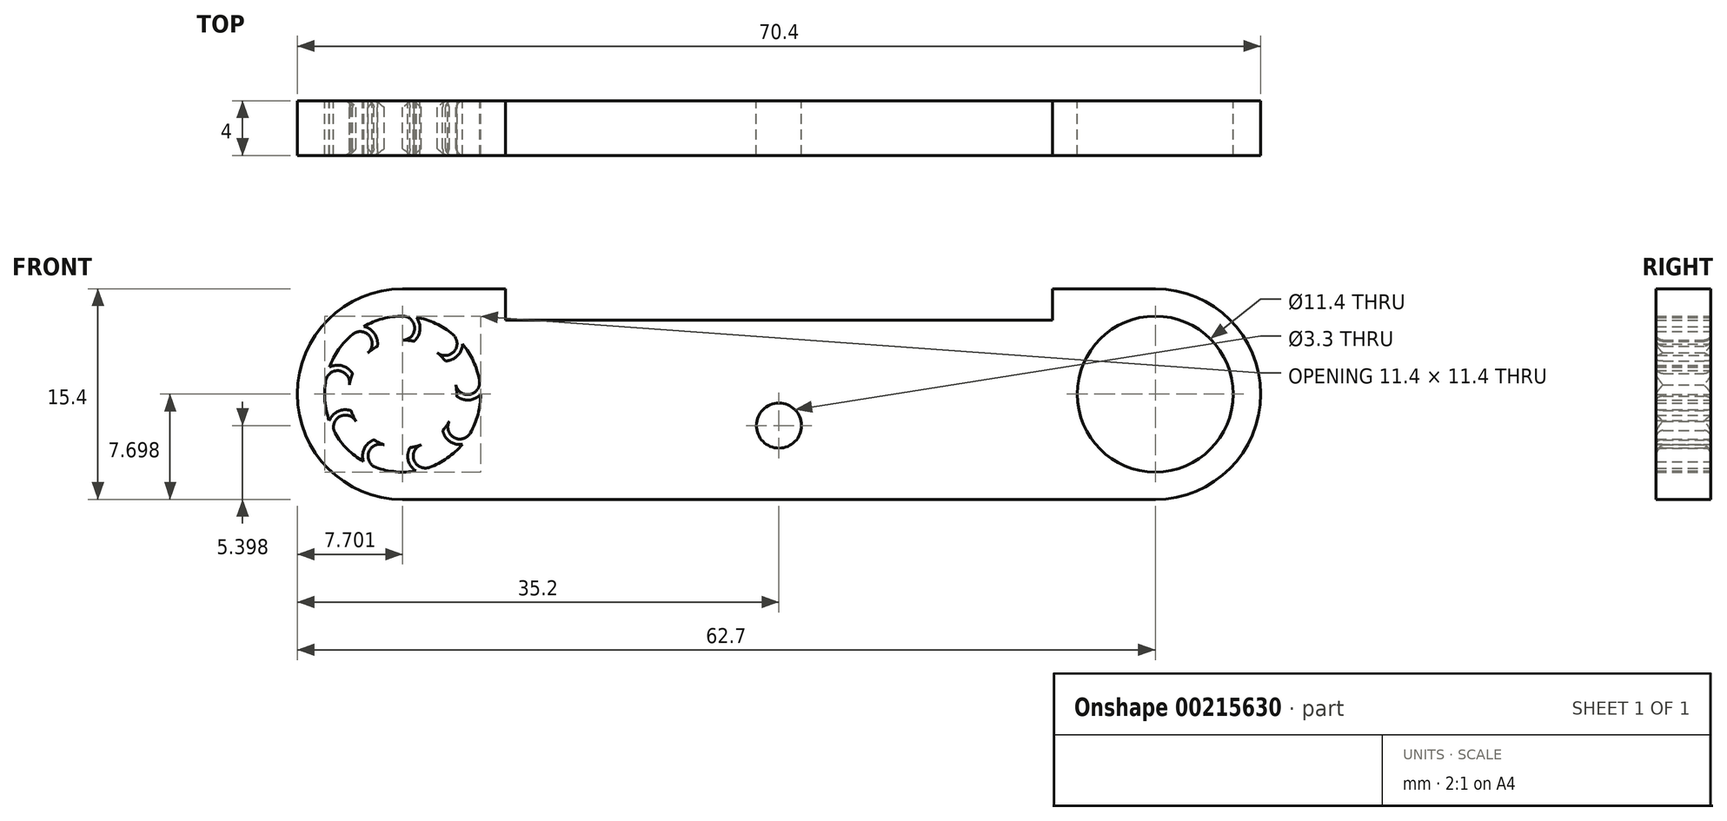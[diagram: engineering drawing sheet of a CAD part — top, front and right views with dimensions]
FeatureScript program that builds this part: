
annotation { "Feature Type Name" : "Feature", "Feature Type Description" : "" }
export const myFeature = defineFeature(function(context is Context, id is Id, definition is map)
    precondition{}
    {
        {
            var Q0;
            Q0=qCreatedBy(makeId("Front.planeOp"),FACE);
            var sketch = newSketch(context, id + "F0", { "sketchPlane" : qUnion([Q0])});
            skLineSegment(sketch, "E0", {"start": v(-27.5, -12.7) * mm, "end": v(0, -12.7) * mm});
            skLineSegment(sketch, "E1", {"start": v(0, -12.7) * mm, "end": v(27.5, -12.7) * mm});
            skCircle(sketch, "E2", {"center": v(-27.5, -12.7) * mm, "radius": 3.8 * mm});
            skCircle(sketch, "E3", {"center": v(27.5, -12.7) * mm, "radius": 3.8 * mm, "construction": true});
            skCircle(sketch, "E4", {"center": v(-27.5, -12.7) * mm, "radius": 5.7 * mm});
            skCircle(sketch, "E5", {"center": v(27.5, -12.7) * mm, "radius": 5.7 * mm});
            skCircle(sketch, "E6", {"center": v(-27.5, -12.7) * mm, "radius": 7.7 * mm});
            skCircle(sketch, "E7", {"center": v(27.5, -12.7) * mm, "radius": 7.7 * mm});
            skLineSegment(sketch, "E8", {"start": v(-27.5, -8.9) * mm, "end": v(-27.5, -7) * mm, "construction": true});
            skLineSegment(sketch, "E9.bottom", {"start": v(-27.5, -5) * mm, "end": v(27.5, -5) * mm});
            skPoint(sketch, "E10", {"position": v(0, -5) * mm});
            skLineSegment(sketch, "E11", {"start": v(27.5, -20.4) * mm, "end": v(-27.5, -20.4) * mm});
            skSolve(sketch);
        }
        {
            var Q0;
            Q0=qSketchRegion(id+"F0",true);
            extrude(context, id + "F1", {"entities" : qUnion([Q0]), "depth" : (4) * mm});
        }
        {
            var Q0;
            Q0=makeQuery(id+"F1.opExtrude","CAP_FACE",FACE,{"disambiguationData":[OSD([sQuery(id+"F0.wireOp",EDGE,"E4"),sQuery(id+"F0.wireOp",EDGE,"E5"),sQuery(id+"F0.wireOp",EDGE,"E6"),sQuery(id+"F0.wireOp",EDGE,"E7"),sQuery(id+"F0.wireOp",EDGE,"E9.bottom"),sQuery(id+"F0.wireOp",EDGE,"E9.top"),sQuery(id+"F0.wireOp",EDGE,"E9.left"),sQuery(id+"F0.wireOp",EDGE,"E9.right")])],"isStart":true});
            var sketch = newSketch(context, id + "F2", { "sketchPlane" : qUnion([Q0])});
            skCircle(sketch, "E12.0", {"center": v(27.5, -12.7) * mm, "radius": 5.7 * mm});
            skCircle(sketch, "E13", {"center": v(27.5, -12.7) * mm, "radius": 3.95 * mm});
            skLineSegment(sketch, "E14", {"start": v(27.5, -12.7) * mm, "end": v(27.5, -7) * mm, "construction": true});
            skArc(sketch, "E15", {"start": v(27.5, -7) * mm, "mid": v(26.62, -7.87) * mm, "end": v(27.5, -8.74) * mm});
            skArc(sketch, "E16", {"start": v(27.5, -6.6) * mm, "mid": v(26.3, -7.42) * mm, "end": v(26.67, -8.83) * mm});
            skArc(sketch, "E17.1.0", {"start": v(23.58, -8.02) * mm, "mid": v(23.2, -9.42) * mm, "end": v(24.38, -10.27) * mm});
            skArc(sketch, "E17.1.1", {"start": v(23.84, -8.33) * mm, "mid": v(23.73, -9.56) * mm, "end": v(24.96, -9.67) * mm});
            skArc(sketch, "E17.2.0", {"start": v(21.5, -11.63) * mm, "mid": v(22.1, -12.95) * mm, "end": v(23.55, -12.84) * mm});
            skArc(sketch, "E17.2.1", {"start": v(21.89, -11.7) * mm, "mid": v(22.6, -12.72) * mm, "end": v(23.61, -12) * mm});
            skArc(sketch, "E17.3.0", {"start": v(22.22, -15.74) * mm, "mid": v(23.53, -16.36) * mm, "end": v(24.57, -15.35) * mm});
            skArc(sketch, "E17.3.1", {"start": v(22.56, -15.54) * mm, "mid": v(23.76, -15.86) * mm, "end": v(24.08, -14.67) * mm});
            skArc(sketch, "E17.4.0", {"start": v(25.41, -18.42) * mm, "mid": v(26.82, -18.05) * mm, "end": v(26.96, -16.6) * mm});
            skArc(sketch, "E17.4.1", {"start": v(25.55, -18.05) * mm, "mid": v(26.67, -17.53) * mm, "end": v(26.15, -16.4) * mm});
            skArc(sketch, "E17.5.0", {"start": v(29.59, -18.42) * mm, "mid": v(30.43, -17.24) * mm, "end": v(29.6, -16.04) * mm});
            skArc(sketch, "E17.5.1", {"start": v(29.45, -18.05) * mm, "mid": v(29.97, -16.93) * mm, "end": v(28.85, -16.4) * mm});
            skArc(sketch, "E17.6.0", {"start": v(32.78, -15.74) * mm, "mid": v(32.66, -14.3) * mm, "end": v(31.26, -13.9) * mm});
            skArc(sketch, "E17.6.1", {"start": v(32.44, -15.54) * mm, "mid": v(32.12, -14.35) * mm, "end": v(30.92, -14.67) * mm});
            skArc(sketch, "E17.7.0", {"start": v(33.5, -11.63) * mm, "mid": v(32.48, -10.6) * mm, "end": v(31.16, -11.2) * mm});
            skArc(sketch, "E17.7.1", {"start": v(33.11, -11.7) * mm, "mid": v(32.1, -11) * mm, "end": v(31.39, -12) * mm});
            skArc(sketch, "E17.8.0", {"start": v(31.42, -8.02) * mm, "mid": v(29.97, -7.89) * mm, "end": v(29.34, -9.2) * mm});
            skArc(sketch, "E17.8.1", {"start": v(31.16, -8.33) * mm, "mid": v(29.93, -8.43) * mm, "end": v(30.04, -9.67) * mm});
            skSolve(sketch);
        }
        {
            var Q0;
            {var subQ0=sQuery(id+"F2.wireOp",EDGE,"E15");Q0=makeQuery(id+"F2.imprint","IMPRINT",FACE,{"disambiguationData":[TD([[makeQuery(id+"F2.imprint","IMPRINT",EDGE,{"derivedFrom":subQ0}),-1.0]])]});}
            var Q1;
            {var subQ0=sQuery(id+"F2.wireOp",EDGE,"E17.1.1");Q1=makeQuery(id+"F2.imprint","IMPRINT",FACE,{"disambiguationData":[TD([[makeQuery(id+"F2.imprint","IMPRINT",EDGE,{"derivedFrom":subQ0}),-1.0]])]});}
            var Q2;
            {var subQ0=sQuery(id+"F2.wireOp",EDGE,"E17.2.1");Q2=makeQuery(id+"F2.imprint","IMPRINT",FACE,{"disambiguationData":[TD([[makeQuery(id+"F2.imprint","IMPRINT",EDGE,{"derivedFrom":subQ0}),-1.0]])]});}
            var Q3;
            {var subQ0=sQuery(id+"F2.wireOp",EDGE,"E17.3.1");Q3=makeQuery(id+"F2.imprint","IMPRINT",FACE,{"disambiguationData":[TD([[makeQuery(id+"F2.imprint","IMPRINT",EDGE,{"derivedFrom":subQ0}),-1.0]])]});}
            var Q4;
            {var subQ0=sQuery(id+"F2.wireOp",EDGE,"E17.4.1");Q4=makeQuery(id+"F2.imprint","IMPRINT",FACE,{"disambiguationData":[TD([[makeQuery(id+"F2.imprint","IMPRINT",EDGE,{"derivedFrom":subQ0}),-1.0]])]});}
            var Q5;
            {var subQ0=sQuery(id+"F2.wireOp",EDGE,"E17.5.1");Q5=makeQuery(id+"F2.imprint","IMPRINT",FACE,{"disambiguationData":[TD([[makeQuery(id+"F2.imprint","IMPRINT",EDGE,{"derivedFrom":subQ0}),-1.0]])]});}
            var Q6;
            {var subQ0=sQuery(id+"F2.wireOp",EDGE,"E17.6.1");Q6=makeQuery(id+"F2.imprint","IMPRINT",FACE,{"disambiguationData":[TD([[makeQuery(id+"F2.imprint","IMPRINT",EDGE,{"derivedFrom":subQ0}),-1.0]])]});}
            var Q7;
            {var subQ0=sQuery(id+"F2.wireOp",EDGE,"E17.7.1");Q7=makeQuery(id+"F2.imprint","IMPRINT",FACE,{"disambiguationData":[TD([[makeQuery(id+"F2.imprint","IMPRINT",EDGE,{"derivedFrom":subQ0}),-1.0]])]});}
            var Q8;
            {var subQ0=sQuery(id+"F2.wireOp",EDGE,"E17.8.1");Q8=makeQuery(id+"F2.imprint","IMPRINT",FACE,{"disambiguationData":[TD([[makeQuery(id+"F2.imprint","IMPRINT",EDGE,{"derivedFrom":subQ0}),-1.0]])]});}
            var Q9;
            Q9=makeQuery(id+"F1.opExtrude","CAP_FACE",FACE,{"disambiguationData":[OSD([sQuery(id+"F0.wireOp",EDGE,"E4"),sQuery(id+"F0.wireOp",EDGE,"E5"),sQuery(id+"F0.wireOp",EDGE,"E6"),sQuery(id+"F0.wireOp",EDGE,"E7"),sQuery(id+"F0.wireOp",EDGE,"E9.bottom"),sQuery(id+"F0.wireOp",EDGE,"E9.top"),sQuery(id+"F0.wireOp",EDGE,"E9.left"),sQuery(id+"F0.wireOp",EDGE,"E9.right")])],"isStart":false});
            extrude(context, id + "F3", {"entities" : qUnion([Q0, Q1, Q2, Q3, Q4, Q5, Q6, Q7, Q8]), "operationType" : NewBodyOperationType.ADD, "endBound" : BoundingType.UP_TO_SURFACE, "oppositeDirection" : true, "endBoundEntityFace" : qUnion([Q9]), "depth" : 25 * mm});
        }
        {
            var Q0;
            {var subQ0=sQuery(id+"F2.wireOp",EDGE,"E17.2.1");var subQ1=sQuery(id+"F2.wireOp",EDGE,"E17.2.0");var subQ2=sQuery(id+"F2.wireOp",EDGE,"E13");var subQ3=sQuery(id+"F2.wireOp",EDGE,"E12.0");var subQ4=sQuery(id+"F2.wireOp",EDGE,"E17.3.1");var subQ5=sQuery(id+"F2.wireOp",EDGE,"E17.3.0");var subQ6=sQuery(id+"F2.wireOp",EDGE,"E17.4.1");var subQ7=sQuery(id+"F2.wireOp",EDGE,"E17.4.0");var subQ8=sQuery(id+"F2.wireOp",EDGE,"E17.5.1");var subQ9=sQuery(id+"F2.wireOp",EDGE,"E17.5.0");var subQ10=sQuery(id+"F2.wireOp",EDGE,"E17.6.1");var subQ11=sQuery(id+"F2.wireOp",EDGE,"E17.6.0");var subQ12=sQuery(id+"F2.wireOp",EDGE,"E17.7.1");var subQ13=sQuery(id+"F2.wireOp",EDGE,"E17.7.0");var subQ14=sQuery(id+"F2.wireOp",EDGE,"E17.8.1");var subQ15=sQuery(id+"F2.wireOp",EDGE,"E17.8.0");var subQ16=sQuery(id+"F2.wireOp",EDGE,"E16");var subQ17=sQuery(id+"F2.wireOp",EDGE,"E15");var subQ18=sQuery(id+"F2.wireOp",EDGE,"E17.1.1");var subQ19=sQuery(id+"F2.wireOp",EDGE,"E17.1.0");Q0=makeQuery(id+"FG6rSbF2kgmWDMH_1.1.F3.boolean.opBoolean","MERGE",FACE,{"derivedFrom":[makeQuery(id+"F3.boolean.opBoolean","MERGE",FACE,{"derivedFrom":[makeQuery(id+"F1.opExtrude","CAP_FACE",FACE,{"disambiguationData":[OSD([sQuery(id+"F0.wireOp",EDGE,"E0"),sQuery(id+"F0.wireOp",EDGE,"E1"),sQuery(id+"F0.wireOp",EDGE,"E4"),sQuery(id+"F0.wireOp",EDGE,"E5"),sQuery(id+"F0.wireOp",EDGE,"E6"),sQuery(id+"F0.wireOp",EDGE,"E7"),sQuery(id+"F0.wireOp",EDGE,"E9.bottom")])],"isStart":true}),makeQuery(id+"F3.opExtrude","CAP_FACE",FACE,{"disambiguationData":[OSD([subQ3,subQ2,subQ19,subQ18])],"isStart":true}),makeQuery(id+"F3.opExtrude","CAP_FACE",FACE,{"disambiguationData":[OSD([subQ3,subQ2,subQ17,subQ16])],"isStart":true}),makeQuery(id+"F3.opExtrude","CAP_FACE",FACE,{"disambiguationData":[OSD([subQ3,subQ2,subQ15,subQ14])],"isStart":true}),makeQuery(id+"F3.opExtrude","CAP_FACE",FACE,{"disambiguationData":[OSD([subQ3,subQ2,subQ13,subQ12])],"isStart":true}),makeQuery(id+"F3.opExtrude","CAP_FACE",FACE,{"disambiguationData":[OSD([subQ3,subQ2,subQ11,subQ10])],"isStart":true}),makeQuery(id+"F3.opExtrude","CAP_FACE",FACE,{"disambiguationData":[OSD([subQ3,subQ2,subQ9,subQ8])],"isStart":true}),makeQuery(id+"F3.opExtrude","CAP_FACE",FACE,{"disambiguationData":[OSD([subQ3,subQ2,subQ7,subQ6])],"isStart":true}),makeQuery(id+"F3.opExtrude","CAP_FACE",FACE,{"disambiguationData":[OSD([subQ3,subQ2,subQ5,subQ4])],"isStart":true}),makeQuery(id+"F3.opExtrude","CAP_FACE",FACE,{"disambiguationData":[OSD([subQ3,subQ2,subQ1,subQ0])],"isStart":true})]}),makeQuery(id+"FG6rSbF2kgmWDMH_1.1.F3.opExtrude","CAP_FACE",FACE,{"disambiguationData":[OSD([subQ3,subQ2,subQ19,subQ18])],"isStart":true}),makeQuery(id+"FG6rSbF2kgmWDMH_1.1.F3.opExtrude","CAP_FACE",FACE,{"disambiguationData":[OSD([subQ3,subQ2,subQ17,subQ16])],"isStart":true}),makeQuery(id+"FG6rSbF2kgmWDMH_1.1.F3.opExtrude","CAP_FACE",FACE,{"disambiguationData":[OSD([subQ3,subQ2,subQ15,subQ14])],"isStart":true}),makeQuery(id+"FG6rSbF2kgmWDMH_1.1.F3.opExtrude","CAP_FACE",FACE,{"disambiguationData":[OSD([subQ3,subQ2,subQ13,subQ12])],"isStart":true}),makeQuery(id+"FG6rSbF2kgmWDMH_1.1.F3.opExtrude","CAP_FACE",FACE,{"disambiguationData":[OSD([subQ3,subQ2,subQ11,subQ10])],"isStart":true}),makeQuery(id+"FG6rSbF2kgmWDMH_1.1.F3.opExtrude","CAP_FACE",FACE,{"disambiguationData":[OSD([subQ3,subQ2,subQ9,subQ8])],"isStart":true}),makeQuery(id+"FG6rSbF2kgmWDMH_1.1.F3.opExtrude","CAP_FACE",FACE,{"disambiguationData":[OSD([subQ3,subQ2,subQ7,subQ6])],"isStart":true}),makeQuery(id+"FG6rSbF2kgmWDMH_1.1.F3.opExtrude","CAP_FACE",FACE,{"disambiguationData":[OSD([subQ3,subQ2,subQ5,subQ4])],"isStart":true}),makeQuery(id+"FG6rSbF2kgmWDMH_1.1.F3.opExtrude","CAP_FACE",FACE,{"disambiguationData":[OSD([subQ3,subQ2,subQ1,subQ0])],"isStart":true})]});}
            var sketch = newSketch(context, id + "F4", { "sketchPlane" : qUnion([Q0])});
            skLineSegment(sketch, "E18.bottom", {"start": v(-20, -5) * mm, "end": v(20, -5) * mm});
            skLineSegment(sketch, "E18.top", {"start": v(-20, -7.3) * mm, "end": v(20, -7.3) * mm});
            skLineSegment(sketch, "E18.left", {"start": v(-20, -5) * mm, "end": v(-20, -7.3) * mm});
            skLineSegment(sketch, "E18.right", {"start": v(20, -5) * mm, "end": v(20, -7.3) * mm});
            skSolve(sketch);
        }
        {
            var Q0;
            Q0 = qSketchRegion(id + "F4", true);
            extrude(context, id + "F5", {"entities" : qUnion([Q0]), "operationType" : NewBodyOperationType.REMOVE, "endBound" : BoundingType.THROUGH_ALL, "oppositeDirection" : true, "depth" : 25 * mm});
        }
        {
            var Q0;
            {var subQ0=sQuery(id+"F2.wireOp",EDGE,"E17.2.1");var subQ1=sQuery(id+"F2.wireOp",EDGE,"E17.2.0");var subQ2=sQuery(id+"F2.wireOp",EDGE,"E13");var subQ3=sQuery(id+"F2.wireOp",EDGE,"E12.0");var subQ4=sQuery(id+"F2.wireOp",EDGE,"E17.3.1");var subQ5=sQuery(id+"F2.wireOp",EDGE,"E17.3.0");var subQ6=sQuery(id+"F2.wireOp",EDGE,"E17.4.1");var subQ7=sQuery(id+"F2.wireOp",EDGE,"E17.4.0");var subQ8=sQuery(id+"F2.wireOp",EDGE,"E17.5.1");var subQ9=sQuery(id+"F2.wireOp",EDGE,"E17.5.0");var subQ10=sQuery(id+"F2.wireOp",EDGE,"E17.6.1");var subQ11=sQuery(id+"F2.wireOp",EDGE,"E17.6.0");var subQ12=sQuery(id+"F2.wireOp",EDGE,"E17.7.1");var subQ13=sQuery(id+"F2.wireOp",EDGE,"E17.7.0");var subQ14=sQuery(id+"F2.wireOp",EDGE,"E17.8.1");var subQ15=sQuery(id+"F2.wireOp",EDGE,"E17.8.0");var subQ16=sQuery(id+"F2.wireOp",EDGE,"E16");var subQ17=sQuery(id+"F2.wireOp",EDGE,"E15");var subQ18=sQuery(id+"F2.wireOp",EDGE,"E17.1.1");var subQ19=sQuery(id+"F2.wireOp",EDGE,"E17.1.0");Q0=makeQuery(id+"FG6rSbF2kgmWDMH_1.1.F3.boolean.opBoolean","MERGE",FACE,{"derivedFrom":[makeQuery(id+"F3.boolean.opBoolean","MERGE",FACE,{"derivedFrom":[makeQuery(id+"F1.opExtrude","CAP_FACE",FACE,{"disambiguationData":[OSD([sQuery(id+"F0.wireOp",EDGE,"E0"),sQuery(id+"F0.wireOp",EDGE,"E1"),sQuery(id+"F0.wireOp",EDGE,"E4"),sQuery(id+"F0.wireOp",EDGE,"E5"),sQuery(id+"F0.wireOp",EDGE,"E6"),sQuery(id+"F0.wireOp",EDGE,"E7"),sQuery(id+"F0.wireOp",EDGE,"E9.bottom")])],"isStart":true}),makeQuery(id+"F3.opExtrude","CAP_FACE",FACE,{"disambiguationData":[OSD([subQ3,subQ2,subQ19,subQ18])],"isStart":true}),makeQuery(id+"F3.opExtrude","CAP_FACE",FACE,{"disambiguationData":[OSD([subQ3,subQ2,subQ17,subQ16])],"isStart":true}),makeQuery(id+"F3.opExtrude","CAP_FACE",FACE,{"disambiguationData":[OSD([subQ3,subQ2,subQ15,subQ14])],"isStart":true}),makeQuery(id+"F3.opExtrude","CAP_FACE",FACE,{"disambiguationData":[OSD([subQ3,subQ2,subQ13,subQ12])],"isStart":true}),makeQuery(id+"F3.opExtrude","CAP_FACE",FACE,{"disambiguationData":[OSD([subQ3,subQ2,subQ11,subQ10])],"isStart":true}),makeQuery(id+"F3.opExtrude","CAP_FACE",FACE,{"disambiguationData":[OSD([subQ3,subQ2,subQ9,subQ8])],"isStart":true}),makeQuery(id+"F3.opExtrude","CAP_FACE",FACE,{"disambiguationData":[OSD([subQ3,subQ2,subQ7,subQ6])],"isStart":true}),makeQuery(id+"F3.opExtrude","CAP_FACE",FACE,{"disambiguationData":[OSD([subQ3,subQ2,subQ5,subQ4])],"isStart":true}),makeQuery(id+"F3.opExtrude","CAP_FACE",FACE,{"disambiguationData":[OSD([subQ3,subQ2,subQ1,subQ0])],"isStart":true})]}),makeQuery(id+"FG6rSbF2kgmWDMH_1.1.F3.opExtrude","CAP_FACE",FACE,{"disambiguationData":[OSD([subQ3,subQ2,subQ19,subQ18])],"isStart":true}),makeQuery(id+"FG6rSbF2kgmWDMH_1.1.F3.opExtrude","CAP_FACE",FACE,{"disambiguationData":[OSD([subQ3,subQ2,subQ17,subQ16])],"isStart":true}),makeQuery(id+"FG6rSbF2kgmWDMH_1.1.F3.opExtrude","CAP_FACE",FACE,{"disambiguationData":[OSD([subQ3,subQ2,subQ15,subQ14])],"isStart":true}),makeQuery(id+"FG6rSbF2kgmWDMH_1.1.F3.opExtrude","CAP_FACE",FACE,{"disambiguationData":[OSD([subQ3,subQ2,subQ13,subQ12])],"isStart":true}),makeQuery(id+"FG6rSbF2kgmWDMH_1.1.F3.opExtrude","CAP_FACE",FACE,{"disambiguationData":[OSD([subQ3,subQ2,subQ11,subQ10])],"isStart":true}),makeQuery(id+"FG6rSbF2kgmWDMH_1.1.F3.opExtrude","CAP_FACE",FACE,{"disambiguationData":[OSD([subQ3,subQ2,subQ9,subQ8])],"isStart":true}),makeQuery(id+"FG6rSbF2kgmWDMH_1.1.F3.opExtrude","CAP_FACE",FACE,{"disambiguationData":[OSD([subQ3,subQ2,subQ7,subQ6])],"isStart":true}),makeQuery(id+"FG6rSbF2kgmWDMH_1.1.F3.opExtrude","CAP_FACE",FACE,{"disambiguationData":[OSD([subQ3,subQ2,subQ5,subQ4])],"isStart":true}),makeQuery(id+"FG6rSbF2kgmWDMH_1.1.F3.opExtrude","CAP_FACE",FACE,{"disambiguationData":[OSD([subQ3,subQ2,subQ1,subQ0])],"isStart":true})]});}
            var sketch = newSketch(context, id + "F6", { "sketchPlane" : qUnion([Q0])});
            skCircle(sketch, "E19", {"center": v(0, -15) * mm, "radius": 1.65 * mm});
            skSolve(sketch);
        }
        {
            var Q0;
            Q0 = qSketchRegion(id + "F6", true);
            extrude(context, id + "F7", {"entities" : qUnion([Q0]), "operationType" : NewBodyOperationType.REMOVE, "endBound" : BoundingType.THROUGH_ALL, "oppositeDirection" : true, "depth" : 25 * mm});
        }
        {
            var Q0;
            Q0=makeQuery(id+"F1.opExtrude","CAP_VERTEX",VERTEX,{"disambiguationData":[OSD([sQuery(id+"F0.wireOp",EDGE,"E6"),sQuery(id+"F0.wireOp",EDGE,"E11")])],"isStart":false});
            var Q1;
            Q1=makeQuery(id+"F1.opExtrude","CAP_VERTEX",VERTEX,{"disambiguationData":[OSD([sQuery(id+"F0.wireOp",EDGE,"E6"),sQuery(id+"F0.wireOp",EDGE,"E9.bottom")])],"isStart":false});
            var Q2;
            Q2=makeQuery(id+"F1.opExtrude","CAP_VERTEX",VERTEX,{"disambiguationData":[OSD([sQuery(id+"F0.wireOp",EDGE,"E6"),sQuery(id+"F0.wireOp",EDGE,"E9.bottom")])],"isStart":true});
            cPlane(context, id + "F8", {"entities" : qUnion([Q0, Q1, Q2]), "cplaneType" : CPlaneType.THREE_POINT, "offset" : 25 * mm, "width" : 150 * mm, "height" : 150 * mm});
        }
        {
            var Q0;
            Q0=qCreatedBy(id+"F8.planeOp",FACE);
            var sketch = newSketch(context, id + "F9", { "sketchPlane" : qUnion([Q0])});
            skLineSegment(sketch, "E20.0", {"start": v(-4, -7) * mm, "end": v(-4, -8.24) * mm});
            skLineSegment(sketch, "E21.0", {"start": v(-3.5, -8.74) * mm, "end": v(-0.5, -8.74) * mm});
            skLineSegment(sketch, "E22.0", {"start": v(0, -8.24) * mm, "end": v(0, -5) * mm});
            skPoint(sketch, "E23.newPointA", {"position": v(0, -20.4) * mm});
            skPoint(sketch, "E23.newPointB", {"position": v(0, -8.74) * mm});
            skArc(sketch, "E23.filletArc", {"start": v(-0.5, -8.74) * mm, "mid": v(-0.15, -8.6) * mm, "end": v(0, -8.24) * mm});
            skPoint(sketch, "E24.visualSharp", {"position": v(-4, -8.74) * mm});
            skArc(sketch, "E24.filletArc", {"start": v(-4, -8.24) * mm, "mid": v(-3.85, -8.6) * mm, "end": v(-3.5, -8.74) * mm});
            skLineSegment(sketch, "E25", {"start": v(-3.5, -8.74) * mm, "end": v(-4, -8.74) * mm});
            skLineSegment(sketch, "E26", {"start": v(-0.5, -8.74) * mm, "end": v(0, -8.74) * mm});
            skLineSegment(sketch, "E27", {"start": v(-4, -8.74) * mm, "end": v(-4, -8.24) * mm});
            skLineSegment(sketch, "E28", {"start": v(0, -8.74) * mm, "end": v(0, -8.24) * mm});
            skSolve(sketch);
        }
        {
            var Q0;
            Q0 = qSketchRegion(id + "F9", true);
            var Q1;
            {var subQ13=sQuery(id+"F0.wireOp",EDGE,"E4");var subQ24=sQuery(id+"F2.wireOp",EDGE,"E16");Q1=makeQuery(id+"F3.boolean.opBoolean","SPLIT",FACE,{"disambiguationData":[TD([makeQuery(id+"F3.opExtrude","SWEPT_FACE",FACE,{"disambiguationData":[OSD([subQ24])]})])],"derivedFrom":makeQuery(id+"F1.opExtrude","SWEPT_FACE",FACE,{"disambiguationData":[OSD([subQ13])]})});}
            revolve(context, id + "F10", {"operationType" : NewBodyOperationType.REMOVE, "entities" : qUnion([Q0]), "axis" : qUnion([Q1]), "revolveType" : RevolveType.FULL, "oppositeDirection" : true});
        }
    });
